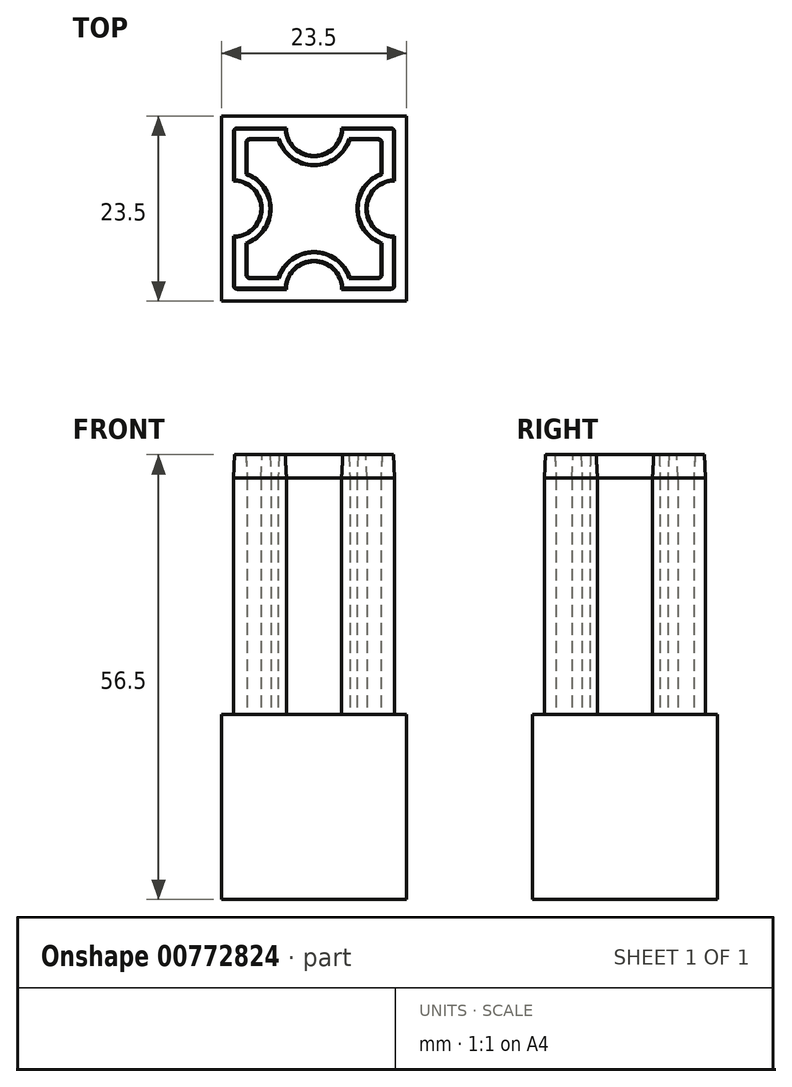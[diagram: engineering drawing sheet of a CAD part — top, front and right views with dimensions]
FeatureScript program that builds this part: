
annotation { "Feature Type Name" : "Feature", "Feature Type Description" : "" }
export const myFeature = defineFeature(function(context is Context, id is Id, definition is map)
    precondition{}
    {
        {
            var Q0;
            Q0=qCreatedBy(makeId("Top.planeOp"),FACE);
            var sketch = newSketch(context, id + "F0", { "sketchPlane" : qUnion([Q0])});
            skLineSegment(sketch, "E0.bottom", {"start": v(-11.75, 11.75) * mm, "end": v(11.75, 11.75) * mm});
            skLineSegment(sketch, "E0.top", {"start": v(-11.75, -11.75) * mm, "end": v(11.75, -11.75) * mm});
            skLineSegment(sketch, "E0.left", {"start": v(-11.75, 11.75) * mm, "end": v(-11.75, -11.75) * mm});
            skLineSegment(sketch, "E0.right", {"start": v(11.75, 11.75) * mm, "end": v(11.75, -11.75) * mm});
            skPoint(sketch, "E0.middle", {"position": v(0, 0) * mm});
            skSolve(sketch);
        }
        {
            var Q0;
            Q0 = qSketchRegion(id + "F0", true);
            extrude(context, id + "F1", {"entities" : qUnion([Q0]), "depth" : 23.5 * mm, "offsetDistance" : 25 * mm});
        }
        {
            var Q0;
            Q0=makeQuery(id+"F1.opExtrude","CAP_FACE",FACE,{"disambiguationData":[OSD([sQuery(id+"F0.wireOp",EDGE,"E0.bottom"),sQuery(id+"F0.wireOp",EDGE,"E0.top"),sQuery(id+"F0.wireOp",EDGE,"E0.left"),sQuery(id+"F0.wireOp",EDGE,"E0.right")])],"isStart":false});
            var sketch = newSketch(context, id + "F2", { "sketchPlane" : qUnion([Q0])});
            skPoint(sketch, "E1.middle", {"position": v(0, 0) * mm});
            skArc(sketch, "E2", {"start": v(-3.5, 10.25) * mm, "mid": v(0, 6.75) * mm, "end": v(3.5, 10.25) * mm});
            skArc(sketch, "E3", {"start": v(-10.25, -3.5) * mm, "mid": v(-6.75, 0) * mm, "end": v(-10.25, 3.5) * mm});
            skArc(sketch, "E4", {"start": v(3.5, -10.25) * mm, "mid": v(0, -6.75) * mm, "end": v(-3.5, -10.25) * mm});
            skArc(sketch, "E5", {"start": v(10.25, 3.5) * mm, "mid": v(6.75, 0) * mm, "end": v(10.25, -3.5) * mm});
            skLineSegment(sketch, "E6", {"start": v(-10.25, 3.5) * mm, "end": v(-10.25, 9.75) * mm});
            skLineSegment(sketch, "E7", {"start": v(-9.75, 10.25) * mm, "end": v(-3.5, 10.25) * mm});
            skLineSegment(sketch, "E8", {"start": v(3.5, 10.25) * mm, "end": v(9.75, 10.25) * mm});
            skLineSegment(sketch, "E9", {"start": v(10.25, 9.75) * mm, "end": v(10.25, 3.5) * mm});
            skLineSegment(sketch, "E10", {"start": v(10.25, -3.5) * mm, "end": v(10.25, -9.75) * mm});
            skLineSegment(sketch, "E11", {"start": v(10.25, -10.25) * mm, "end": v(3.5, -10.25) * mm});
            skLineSegment(sketch, "E12", {"start": v(-3.5, -10.25) * mm, "end": v(-10.25, -10.25) * mm});
            skLineSegment(sketch, "E13", {"start": v(-10.25, -10.25) * mm, "end": v(-10.25, -3.5) * mm});
            skArc(sketch, "E14", {"start": v(-8.5, -4.47) * mm, "mid": v(-5.45, 0) * mm, "end": v(-8.5, 4.47) * mm});
            skArc(sketch, "E15", {"start": v(-4.56, 8.75) * mm, "mid": v(0, 5.45) * mm, "end": v(4.56, 8.75) * mm});
            skArc(sketch, "E16", {"start": v(8.5, 4.47) * mm, "mid": v(5.45, 0) * mm, "end": v(8.5, -4.47) * mm});
            skArc(sketch, "E17", {"start": v(4.56, -8.75) * mm, "mid": v(0, -5.45) * mm, "end": v(-4.56, -8.75) * mm});
            skPoint(sketch, "E18.visualSharp", {"position": v(-8.5, 8.75) * mm});
            skArc(sketch, "E18.filletArc", {"start": v(-8.1, 8.75) * mm, "mid": v(-8.38, 8.63) * mm, "end": v(-8.5, 8.35) * mm});
            skPoint(sketch, "E19.visualSharp", {"position": v(8.5, 8.75) * mm});
            skArc(sketch, "E19.filletArc", {"start": v(8.5, 8.35) * mm, "mid": v(8.38, 8.63) * mm, "end": v(8.1, 8.75) * mm});
            skPoint(sketch, "E20.visualSharp", {"position": v(-8.5, -8.75) * mm});
            skArc(sketch, "E20.filletArc", {"start": v(-8.5, -8.35) * mm, "mid": v(-8.38, -8.63) * mm, "end": v(-8.1, -8.75) * mm});
            skPoint(sketch, "E21.visualSharp", {"position": v(8.5, -8.75) * mm});
            skArc(sketch, "E21.filletArc", {"start": v(8.1, -8.75) * mm, "mid": v(8.38, -8.63) * mm, "end": v(8.5, -8.35) * mm});
            skPoint(sketch, "E22.visualSharp", {"position": v(-10.25, 10.25) * mm});
            skArc(sketch, "E22.filletArc", {"start": v(-9.75, 10.25) * mm, "mid": v(-10.1, 10.1) * mm, "end": v(-10.25, 9.75) * mm});
            skPoint(sketch, "E23.visualSharp", {"position": v(10.25, 10.25) * mm});
            skArc(sketch, "E23.filletArc", {"start": v(10.25, 9.75) * mm, "mid": v(10.1, 10.1) * mm, "end": v(9.75, 10.25) * mm});
            skPoint(sketch, "E24.visualSharp", {"position": v(-10.25, -10.25) * mm});
            skArc(sketch, "E24.filletArc", {"start": v(-10.25, -9.75) * mm, "mid": v(-10.1, -10.1) * mm, "end": v(-9.75, -10.25) * mm});
            skPoint(sketch, "E25.visualSharp", {"position": v(10.25, -10.25) * mm});
            skArc(sketch, "E25.filletArc", {"start": v(9.75, -10.25) * mm, "mid": v(10.1, -10.1) * mm, "end": v(10.25, -9.75) * mm});
            skLineSegment(sketch, "E26", {"start": v(9.75, -10.25) * mm, "end": v(3.5, -10.25) * mm});
            skLineSegment(sketch, "E27", {"start": v(-3.5, -10.25) * mm, "end": v(-9.75, -10.25) * mm});
            skLineSegment(sketch, "E28", {"start": v(-10.25, -9.75) * mm, "end": v(-10.25, -3.5) * mm});
            skLineSegment(sketch, "E29", {"start": v(-8.1, 8.75) * mm, "end": v(-4.56, 8.75) * mm});
            skLineSegment(sketch, "E30", {"start": v(4.56, 8.75) * mm, "end": v(8.1, 8.75) * mm});
            skLineSegment(sketch, "E31", {"start": v(8.5, 8.35) * mm, "end": v(8.5, 4.47) * mm});
            skLineSegment(sketch, "E32", {"start": v(8.5, -4.47) * mm, "end": v(8.5, -8.35) * mm});
            skLineSegment(sketch, "E33", {"start": v(8.1, -8.75) * mm, "end": v(4.56, -8.75) * mm});
            skLineSegment(sketch, "E34", {"start": v(-4.56, -8.75) * mm, "end": v(-8.1, -8.75) * mm});
            skLineSegment(sketch, "E35", {"start": v(-8.5, -8.35) * mm, "end": v(-8.5, -4.47) * mm});
            skLineSegment(sketch, "E36", {"start": v(-8.5, 4.47) * mm, "end": v(-8.5, 8.35) * mm});
            skSolve(sketch);
        }
        {
            var Q0;
            Q0=makeQuery(id+"F2.imprint","IMPRINT",FACE,{"disambiguationData":[TD([[makeQuery(id+"F2.imprint","IMPRINT",EDGE,{"derivedFrom":sQuery(id+"F2.wireOp",EDGE,"E2")}),-1.0]])]});
            extrude(context, id + "F3", {"entities" : qUnion([Q0]), "operationType" : NewBodyOperationType.ADD, "depth" : 30 * mm, "offsetDistance" : 25 * mm});
        }
        {
            var Q0;
            Q0=makeQuery(id+"F3.opExtrude","CAP_FACE",FACE,{"disambiguationData":[OSD([sQuery(id+"F2.wireOp",EDGE,"E2"),sQuery(id+"F2.wireOp",EDGE,"E3"),sQuery(id+"F2.wireOp",EDGE,"E4"),sQuery(id+"F2.wireOp",EDGE,"E5"),sQuery(id+"F2.wireOp",EDGE,"E14"),sQuery(id+"F2.wireOp",EDGE,"E15"),sQuery(id+"F2.wireOp",EDGE,"E16"),sQuery(id+"F2.wireOp",EDGE,"E17"),sQuery(id+"F2.wireOp",EDGE,"E18.filletArc"),sQuery(id+"F2.wireOp",EDGE,"E19.filletArc"),sQuery(id+"F2.wireOp",EDGE,"E20.filletArc"),sQuery(id+"F2.wireOp",EDGE,"E21.filletArc"),sQuery(id+"F2.wireOp",EDGE,"E22.filletArc"),sQuery(id+"F2.wireOp",EDGE,"E23.filletArc"),sQuery(id+"F2.wireOp",EDGE,"E24.filletArc"),sQuery(id+"F2.wireOp",EDGE,"E25.filletArc"),sQuery(id+"F2.wireOp",EDGE,"E6"),sQuery(id+"F2.wireOp",EDGE,"E7"),sQuery(id+"F2.wireOp",EDGE,"E8"),sQuery(id+"F2.wireOp",EDGE,"E9"),sQuery(id+"F2.wireOp",EDGE,"E10"),sQuery(id+"F2.wireOp",EDGE,"E26"),sQuery(id+"F2.wireOp",EDGE,"E27"),sQuery(id+"F2.wireOp",EDGE,"E28"),sQuery(id+"F2.wireOp",EDGE,"E29"),sQuery(id+"F2.wireOp",EDGE,"E30"),sQuery(id+"F2.wireOp",EDGE,"E31"),sQuery(id+"F2.wireOp",EDGE,"E32"),sQuery(id+"F2.wireOp",EDGE,"E33"),sQuery(id+"F2.wireOp",EDGE,"E34"),sQuery(id+"F2.wireOp",EDGE,"E35"),sQuery(id+"F2.wireOp",EDGE,"E36")])],"isStart":false});
            extrude(context, id + "F4", {"entities" : qUnion([Q0]), "operationType" : NewBodyOperationType.ADD, "depth" : 3 * mm, "offsetDistance" : 25 * mm, "hasDraft" : true, "draftAngle" : 3 * degree, "draftPullDirection" : true});
        }
    });
